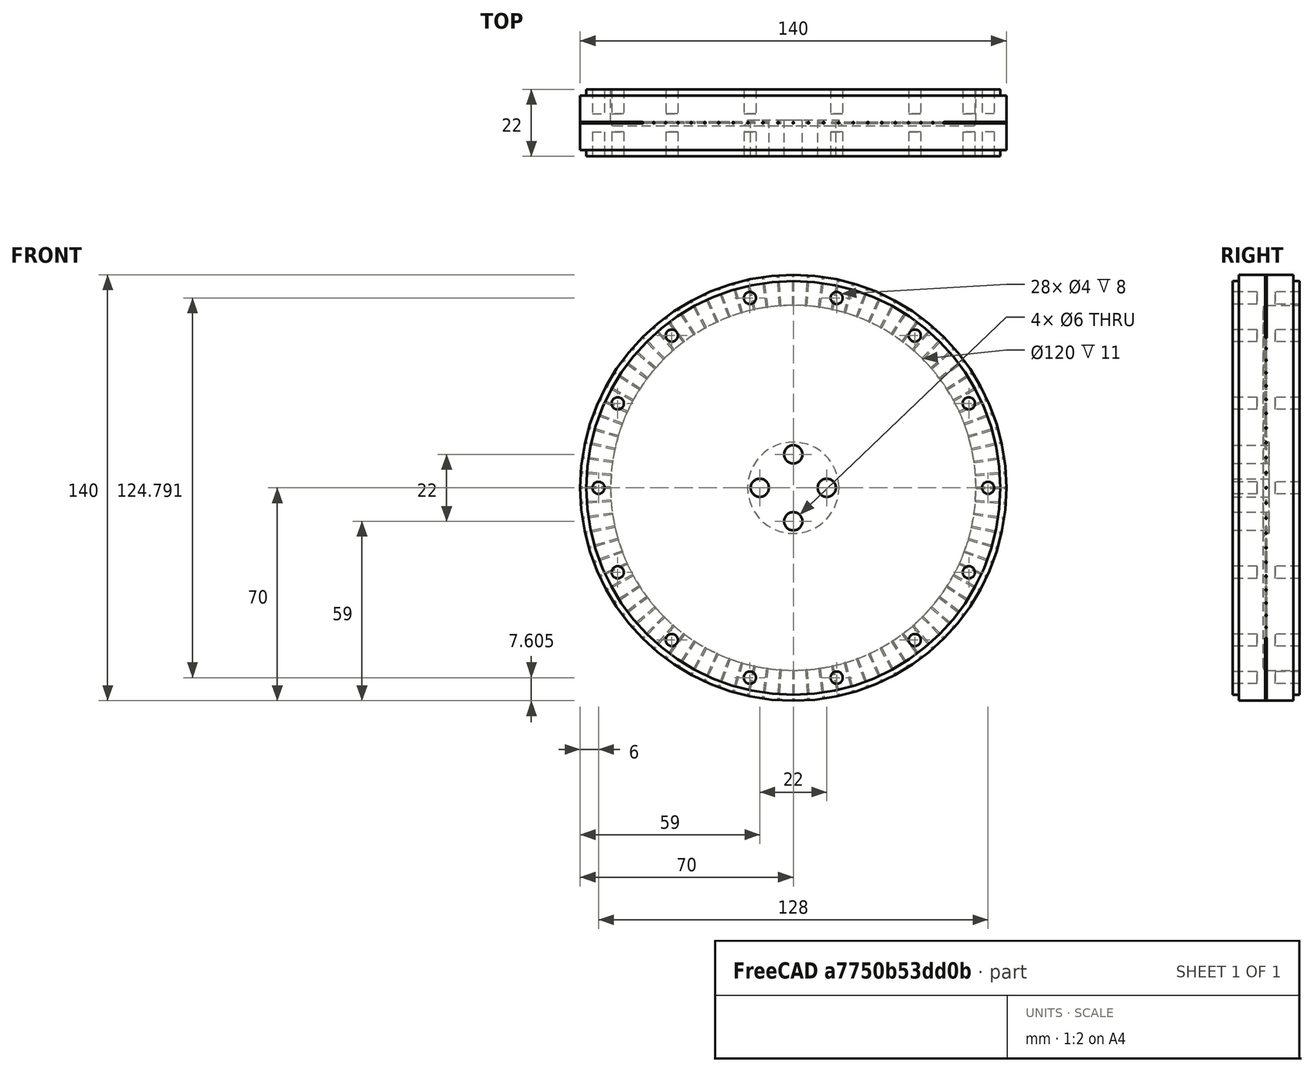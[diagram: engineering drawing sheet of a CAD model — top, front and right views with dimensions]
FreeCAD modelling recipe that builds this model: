
FCSTD DOCUMENT  (FreeCAD 0.18.4R)
Label: блин002
License: All rights reserved
LicenseURL: http://en.wikipedia.org/wiki/All_rights_reserved
objects: TechDraw::DrawViewDimension×10, Part::Cylinder×3, Part::FeaturePython×3, Sketcher::SketchObject×2, Part::Cut×2, PartDesign::Revolution×1, PartDesign::Hole×1, PartDesign::Body×1, Part::Compound×1, TechDraw::DrawSVGTemplate×1, TechDraw::DrawViewPart×1, TechDraw::DrawViewSection×1, TechDraw::DrawPage×1
note: 16 computed .brp shape members not serialized (recipe doc carries the construction recipe); baked Part::Feature solids carry a one-line shape summary decoded from their .brp

FEATURE [Sketcher::SketchObject] Sketch
  MapMode = 5
  Support = -> [XY_Plane001]
  sketch-geometry (14):
    g0: LineSegment StartX=0 StartY=0 StartZ=0 EndX=0 EndY=12 EndZ=0
    g1: LineSegment StartX=0 StartY=12 StartZ=0 EndX=-15 EndY=12 EndZ=0
    g2: LineSegment StartX=-15 StartY=12 StartZ=0 EndX=-15 EndY=12 EndZ=0
    g3: LineSegment StartX=-17 StartY=10 StartZ=0 EndX=-59 EndY=10 EndZ=0
    g4: LineSegment StartX=-60 StartY=11 StartZ=0 EndX=-60 EndY=22 EndZ=0
    g5: LineSegment StartX=-60 StartY=22 StartZ=0 EndX=-68 EndY=22 EndZ=0
    g6: LineSegment StartX=-68 StartY=22 StartZ=0 EndX=-68 EndY=20 EndZ=0
    g7: LineSegment StartX=-68 StartY=20 StartZ=0 EndX=-70 EndY=20 EndZ=0
    g8: LineSegment StartX=-70 StartY=20 StartZ=0 EndX=-70 EndY=2 EndZ=0
    g9: LineSegment StartX=-70 StartY=2 StartZ=0 EndX=-68 EndY=2 EndZ=0
    g10: LineSegment StartX=-68 StartY=2 StartZ=0 EndX=-68 EndY=0 EndZ=0
    g11: LineSegment StartX=-68 StartY=0 StartZ=0 EndX=0 EndY=0 EndZ=0
    g12: ArcOfCircle CenterX=-59 CenterY=11 CenterZ=0 NormalX=0 NormalY=0 NormalZ=1 AngleXU=0 Radius=1 StartAngle=3.14159 EndAngle=4.71239
    g13: ArcOfCircle CenterX=-17 CenterY=12 CenterZ=0 NormalX=0 NormalY=0 NormalZ=1 AngleXU=0 Radius=2 StartAngle=4.71239 EndAngle=6.28319
  constraints (40):
    c: Coincident(g-1,g0)
    c: PointOnObject(g0,g-2)
    c: Coincident(g0,g1)
    c: Horizontal(g1)
    c: Coincident(g1,g2)
    c: Vertical(g2)
    c: Horizontal(g3)
    c: Vertical(g4)
    c: Coincident(g4,g5)
    c: Horizontal(g5)
    c: Coincident(g5,g6)
    c: Vertical(g6)
    c: Coincident(g6,g7)
    c: Horizontal(g7)
    c: Coincident(g7,g8)
    c: Vertical(g8)
    c: Coincident(g8,g9)
    c: Horizontal(g9)
    c: Coincident(g9,g10)
    c: Vertical(g10)
    c: Coincident(g10,g11)
    c: Horizontal(g11)
    c: Coincident(g0,g11)
    c: DistanceX(g11,g11) = 68
    c: DistanceY(g10,g10) = 2
    c: DistanceX(g9,g9) = 2
    c: DistanceX(g7,g7) = 2
    c: DistanceY(g6,g6) = 2
    c: DistanceY(g8,g8) = 18
    c: DistanceX(g5,g5) = 8
    c: DistanceY(g0,g0) = 12
    c: Tangent(g4,g12) = 1.5708
    c: Tangent(g3,g12) = 1.5708
    c: Tangent(g3,g13) = 1.5708
    c: Radius(g13) = 2
    c: Radius(g12) = 1
    c: DistanceY(g2,g2) = 0
    c: DistanceX(g1,g1) = 15
    c: DistanceY(g3,g1) = 2
    c: DistanceX(g3,g1) = 2
FEATURE [PartDesign::Revolution] Revolution
  Angle = 360
  Axis = (0,1,0)
  Base = (0,0,0)
  Profile = -> Sketch
  ReferenceAxis = -> Sketch [V_Axis]
FEATURE [Sketcher::SketchObject] Sketch001
  MapMode = 5
  Placement = pos=(0,0,0) rot=(1,0,0;1.5708rad)
  Support = -> [XZ_Plane001]
  sketch-geometry (4):
    g0: Circle CenterX=11 CenterY=0 CenterZ=0 NormalX=0 NormalY=0 NormalZ=1 AngleXU=0 Radius=3
    g1: Circle CenterX=-11 CenterY=0 CenterZ=0 NormalX=0 NormalY=0 NormalZ=1 AngleXU=0 Radius=3
    g2: Circle CenterX=0 CenterY=11 CenterZ=0 NormalX=0 NormalY=0 NormalZ=1 AngleXU=0 Radius=3
    g3: Circle CenterX=0 CenterY=-11 CenterZ=0 NormalX=0 NormalY=0 NormalZ=1 AngleXU=0 Radius=3
  constraints (12):
    c: PointOnObject(g0,g-1)
    c: PointOnObject(g1,g-1)
    c: PointOnObject(g2,g-2)
    c: PointOnObject(g3,g-2)
    c: Diameter(g2) = 6
    c: Diameter(g0) = 6
    c: Diameter(g3) = 6
    c: Diameter(g1) = 6
    c: DistanceX(g1,g-1) = 11
    c: DistanceX(g-1,g0) = 11
    c: DistanceY(g3,g-1) = 11
    c: DistanceY(g-1,g2) = 11
FEATURE [PartDesign::Hole] Hole
  BaseFeature = -> Revolution
  Depth = 25
  DepthType = 0
  Diameter = 6
  DrillPoint = 1
  DrillPointAngle = 118
  HoleCutCountersinkAngle = 90
  HoleCutDepth = 0
  HoleCutDiameter = 0
  HoleCutType = 0
  ModelActualThread = false
  Profile = -> Sketch001
  Tapered = false
  TaperedAngle = 90
  ThreadAngle = 0
  ThreadClass = 0
  ThreadCutOffInner = 0
  ThreadCutOffOuter = 0
  ThreadDirection = 0
  ThreadFit = 0
  ThreadPitch = 0
  ThreadSize = 0
  ThreadType = 0
  Threaded = false
FEATURE [PartDesign::Body] Body001
  Group = -> [Sketch,Revolution,Sketch001,Hole]
  Origin = -> Origin001
  Placement = pos=(0,-25,0) rot=(0,0,1;0rad)
  Tip = -> Hole
FEATURE [Part::Cylinder] Cylinder  label="Цилиндр"
  Angle = 360
  AttacherType = Attacher::AttachEngine3D
  Height = 12
  Placement = pos=(0,-14,59) rot=(0,0,1;0rad)
  Radius = 0.25
FEATURE [Part::FeaturePython] Array  # Draft array (typed FeaturePython)
  Angle = 360
  ArrayType = 1
  Axis = (0,1,0)
  Base = -> Cylinder
  Center = (0,0,0)
  Fuse = false
  IntervalAxis = (0,0,0)
  IntervalX = (1,0,0)
  IntervalY = (0,1,0)
  IntervalZ = (0,0,1)
  NumberPolar = 88
  NumberX = 1
  NumberY = 2
  NumberZ = 1
FEATURE [Part::Cut] Cut
  Base = -> Body001
  Tool = -> Array
FEATURE [Part::Cylinder] Cylinder001  label="Цилиндр001"
  Angle = 360
  AttacherType = Attacher::AttachEngine3D
  Height = 10
  Placement = pos=(64,-1,0) rot=(1,0,0;1.5708rad)
  Radius = 2
FEATURE [Part::FeaturePython] Array001  # Draft array (typed FeaturePython)
  Angle = 360
  ArrayType = 1
  Axis = (0,1,0)
  Base = -> Cylinder001
  Center = (0,0,0)
  Fuse = false
  IntervalAxis = (0,0,0)
  IntervalX = (1,0,0)
  IntervalY = (0,1,0)
  IntervalZ = (0,0,1)
  NumberPolar = 14
  NumberX = 2
  NumberY = 2
  NumberZ = 1
FEATURE [Part::Cylinder] Cylinder002  label="Цилиндр002"
  Angle = 360
  AttacherType = Attacher::AttachEngine3D
  Height = 10
  Placement = pos=(64,-17,0) rot=(1,0,0;1.5708rad)
  Radius = 2
FEATURE [Part::FeaturePython] Array002  # Draft array (typed FeaturePython)
  Angle = 360
  ArrayType = 1
  Axis = (0,1,0)
  Base = -> Cylinder002
  Center = (0,0,0)
  Fuse = false
  IntervalAxis = (0,0,0)
  IntervalX = (1,0,0)
  IntervalY = (0,1,0)
  IntervalZ = (0,0,1)
  NumberPolar = 14
  NumberX = 2
  NumberY = 2
  NumberZ = 1
FEATURE [Part::Compound] Compound
  Links = -> [Array001,Array002]
FEATURE [Part::Cut] Cut001
  Base = -> Cut
  Tool = -> Compound
FEATURE [TechDraw::DrawSVGTemplate] Template
  EditableTexts = Designed_by_Name=Designed by Name; Drawing_number=Drawing number; FC-Date=Date; FC-SC=Scale; FC-SH=Sheet; FC-Title=Title; Subtitle=Subtitle; Weight=Weight
  Height = 210
  Orientation = 1
  Width = 297
FEATURE [TechDraw::DrawViewPart] View
  CoarseView = false
  Direction = (0,1,0)
  Focus = 100
  HardHidden = false
  IsoCount = 0
  IsoHidden = false
  IsoVisible = false
  LockPosition = false
  Perspective = false
  Rotation = 0
  ScaleType = 0
  SeamHidden = false
  SeamVisible = false
  SmoothHidden = false
  SmoothVisible = false
  Source = -> [Cut001]
  X = 207.243
  Y = 128.554
FEATURE [TechDraw::DrawViewSection] Section  label="Section A - A"
  BaseView = -> View
  CoarseView = false
  Direction = (-1,0,0)
  Focus = 100
  FuseBeforeCut = true
  HardHidden = false
  HatchScale = 1
  IsoCount = 0
  IsoHidden = false
  IsoVisible = false
  LockPosition = false
  NameGeomPattern = Diamond
  Perspective = false
  Rotation = 0
  ScaleType = 0
  SeamHidden = false
  SeamVisible = false
  SectionDirection = 1
  SectionNormal = (-1,0,0)
  SectionOrigin = (0,-14,0)
  SectionSymbol = A
  SmoothHidden = false
  SmoothVisible = false
  Source = -> [Cut001]
  X = 59.309
  Y = 127.657
FEATURE [TechDraw::DrawViewDimension] Dimension
  Arbitrary = false
  FormatSpec = ⌀%.2f
  LockPosition = false
  MeasureType = 1
  OverTolerance = 0
  References2D = -> [View]
  Rotation = 0
  ScaleType = 0
  Type = 5
  UnderTolerance = 0
  X = -74.3514
  Y = -67.8243
FEATURE [TechDraw::DrawViewDimension] Dimension001
  Arbitrary = false
  FormatSpec = ⌀%.2f
  LockPosition = false
  MeasureType = 1
  OverTolerance = 0
  References2D = -> [View]
  Rotation = 0
  ScaleType = 0
  Type = 5
  UnderTolerance = 0
  X = -74.3514
  Y = -57.8919
FEATURE [TechDraw::DrawViewDimension] Dimension002
  Arbitrary = false
  FormatSpec = ⌀%.2f
  LockPosition = false
  MeasureType = 1
  OverTolerance = 0
  References2D = -> [View]
  Rotation = 0
  ScaleType = 0
  Type = 5
  UnderTolerance = 0
  X = -74.0676
  Y = -47.3919
FEATURE [TechDraw::DrawViewDimension] Dimension003
  Arbitrary = false
  FormatSpec = ⌀%.2f
  LockPosition = false
  MeasureType = 1
  OverTolerance = 0
  References2D = -> [View]
  Rotation = 0
  ScaleType = 0
  Type = 5
  UnderTolerance = 0
  X = -29.7973
  Y = -28.3784
FEATURE [TechDraw::DrawViewDimension] Dimension004
  Arbitrary = false
  FormatSpec = ⌀%.2f
  LockPosition = false
  MeasureType = 1
  OverTolerance = 0
  References2D = -> [View]
  Rotation = 0
  ScaleType = 0
  Type = 5
  UnderTolerance = 0
  X = -38.3108
  Y = -18.1622
FEATURE [TechDraw::DrawViewDimension] Dimension005
  Arbitrary = false
  FormatSpec = %.2f
  LockPosition = false
  MeasureType = 1
  OverTolerance = 0
  References2D = -> [View]
  Rotation = 0
  ScaleType = 0
  Type = 1
  UnderTolerance = 0
  X = -29.9384
  Y = 23.7173
FEATURE [TechDraw::DrawViewDimension] Dimension006
  Arbitrary = false
  FormatSpec = %.2f
  LockPosition = false
  MeasureType = 1
  OverTolerance = 0
  References2D = -> [Section]
  Rotation = 0
  ScaleType = 0
  Type = 1
  UnderTolerance = 0
  X = 35.0811
  Y = 3.08108
FEATURE [TechDraw::DrawViewDimension] Dimension007
  Arbitrary = false
  FormatSpec = %.2f
  LockPosition = false
  MeasureType = 1
  OverTolerance = 0
  References2D = -> [Section]
  Rotation = 0
  ScaleType = 0
  Type = 1
  UnderTolerance = 0
  X = 34.6622
  Y = -39.7027
FEATURE [TechDraw::DrawViewDimension] Dimension008
  Arbitrary = false
  FormatSpec = %.2f
  LockPosition = false
  MeasureType = 1
  OverTolerance = 0
  References2D = -> [Section]
  Rotation = 0
  ScaleType = 0
  Type = 1
  UnderTolerance = 0
  X = 4.39428
  Y = -92.9054
FEATURE [TechDraw::DrawViewDimension] Dimension009
  Arbitrary = false
  FormatSpec = %.2f
  LockPosition = false
  MeasureType = 1
  OverTolerance = 0
  References2D = -> [Section]
  Rotation = 0
  ScaleType = 0
  Type = 1
  UnderTolerance = 0
  X = 34.6216
  Y = -79.461
FEATURE [TechDraw::DrawPage] Page
  KeepUpdated = true
  ProjectionType = 0
  Template = -> Template
  Views = -> [View,Section,Dimension,Dimension001,Dimension002,Dimension003,Dimension004,Dimension005,Dimension006,Dimension007,Dimension008,Dimension009]
